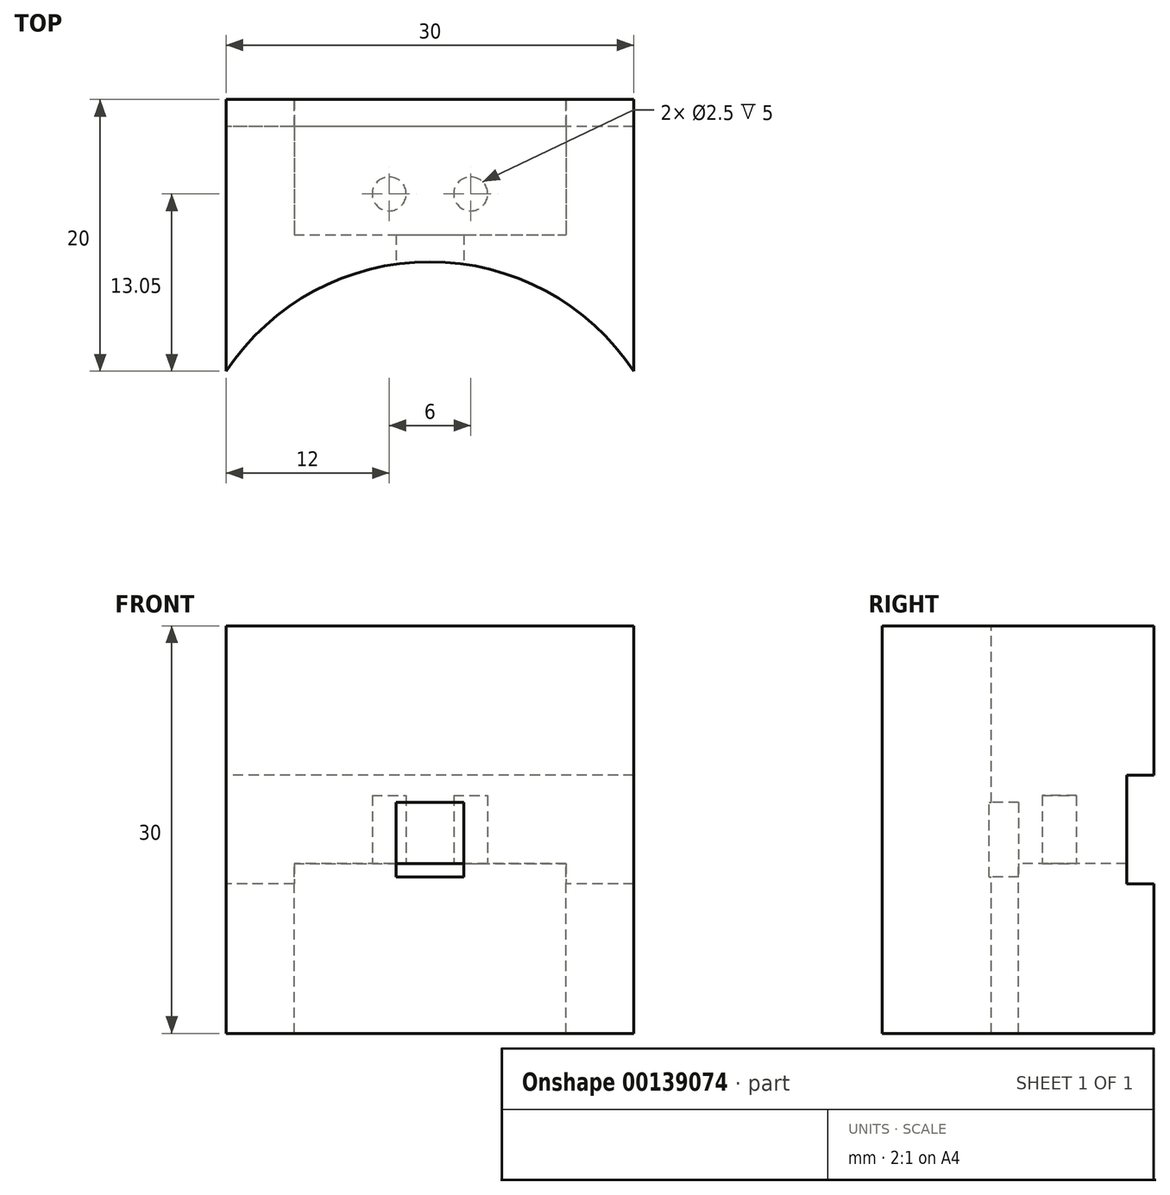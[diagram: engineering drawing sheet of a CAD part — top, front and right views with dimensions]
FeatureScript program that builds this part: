
annotation { "Feature Type Name" : "Feature", "Feature Type Description" : "" }
export const myFeature = defineFeature(function(context is Context, id is Id, definition is map)
    precondition{}
    {
        {
            var Q0;
            Q0=qCreatedBy(makeId("Front.planeOp"),FACE);
            var sketch = newSketch(context, id + "F0", { "sketchPlane" : qUnion([Q0])});
            skLineSegment(sketch, "E0", {"start": v(0, 0) * mm, "end": v(30, 0) * mm});
            skLineSegment(sketch, "E1", {"start": v(30, 0) * mm, "end": v(30, 30) * mm});
            skLineSegment(sketch, "E2", {"start": v(30, 30) * mm, "end": v(0, 30) * mm});
            skLineSegment(sketch, "E3", {"start": v(0, 30) * mm, "end": v(0, 0) * mm});
            skSolve(sketch);
        }
        {
            var Q0;
            Q0 = qSketchRegion(id + "F0", true);
            extrude(context, id + "F1", {"entities" : qUnion([Q0]), "depth" : 20 * mm});
        }
        {
            var Q0;
            Q0=makeQuery(id+"F1.opExtrude","SWEPT_FACE",FACE,{"disambiguationData":[OSD([sQuery(id+"F0.wireOp",EDGE,"E2")])]});
            var sketch = newSketch(context, id + "F2", { "sketchPlane" : qUnion([Q0])});
            skArc(sketch, "E4", {"start": v(30, -20) * mm, "mid": v(15, -11.95) * mm, "end": v(0, -20) * mm});
            skLineSegment(sketch, "E5", {"start": v(0, -20) * mm, "end": v(30, -20) * mm});
            skSolve(sketch);
        }
        {
            var Q0;
            Q0 = qSketchRegion(id + "F2", true);
            extrude(context, id + "F3", {"entities" : qUnion([Q0]), "operationType" : NewBodyOperationType.REMOVE, "endBound" : BoundingType.THROUGH_ALL, "oppositeDirection" : true, "depth" : 25 * mm});
        }
        {
            var Q0;
            Q0=makeQuery(id+"F1.opExtrude","SWEPT_FACE",FACE,{"disambiguationData":[OSD([sQuery(id+"F0.wireOp",EDGE,"E2")])]});
            var sketch = newSketch(context, id + "F4", { "sketchPlane" : qUnion([Q0])});
            skPoint(sketch, "E6", {"position": v(15, -11.95) * mm});
            skSolve(sketch);
        }
        {
            var Q0;
            Q0=qCreatedBy(makeId("Front.planeOp"),FACE);
            var Q1;
            Q1=sQuery(id+"F4.wireOp",VERTEX,"E6");
            cPlane(context, id + "F5", {"entities" : qUnion([Q0, Q1]), "cplaneType" : CPlaneType.PLANE_POINT, "offset" : 25 * mm, "width" : 150 * mm, "height" : 150 * mm});
        }
        {
            var Q0;
            Q0=qCreatedBy(id+"F5.planeOp",FACE);
            cPlane(context, id + "F6", {"entities" : qUnion([Q0]), "cplaneType" : CPlaneType.OFFSET, "offset" : 1 * mm, "width" : 150 * mm, "height" : 150 * mm});
        }
        {
            var Q0;
            Q0=qCreatedBy(id+"F6.planeOp",FACE);
            var sketch = newSketch(context, id + "F7", { "sketchPlane" : qUnion([Q0])});
            skLineSegment(sketch, "E7.bottom", {"start": v(12.5, 17) * mm, "end": v(17.5, 17) * mm});
            skLineSegment(sketch, "E7.top", {"start": v(12.5, 13) * mm, "end": v(17.5, 13) * mm});
            skLineSegment(sketch, "E7.left", {"start": v(12.5, 17) * mm, "end": v(12.5, 13) * mm});
            skLineSegment(sketch, "E7.right", {"start": v(17.5, 17) * mm, "end": v(17.5, 13) * mm});
            skLineSegment(sketch, "E8.0", {"start": v(30, 30) * mm, "end": v(0, 30) * mm, "construction": true});
            skLineSegment(sketch, "E9.0", {"start": v(30, 0) * mm, "end": v(30, 30) * mm, "construction": true});
            skLineSegment(sketch, "E10.0", {"start": v(0, 0) * mm, "end": v(30, 0) * mm, "construction": true});
            skLineSegment(sketch, "E11.0", {"start": v(0, 30) * mm, "end": v(0, 0) * mm, "construction": true});
            skLineSegment(sketch, "E12", {"start": v(15, 0) * mm, "end": v(15, 30) * mm, "construction": true});
            skLineSegment(sketch, "E13", {"start": v(0, 15) * mm, "end": v(30, 15) * mm, "construction": true});
            skSolve(sketch);
        }
        {
            var Q0;
            Q0 = qSketchRegion(id + "F7", true);
            extrude(context, id + "F8", {"entities" : qUnion([Q0]), "operationType" : NewBodyOperationType.REMOVE, "oppositeDirection" : true, "depth" : 3 * mm});
        }
        {
            var Q0;
            Q0=makeQuery(id+"F8.boolean.opBoolean","COPY",FACE,{"derivedFrom":makeQuery(id+"F8.opExtrude","SWEPT_FACE",FACE,{"disambiguationData":[OSD([sQuery(id+"F7.wireOp",EDGE,"E7.top")])]})});
            var sketch = newSketch(context, id + "F9", { "sketchPlane" : qUnion([Q0])});
            skLineSegment(sketch, "E14.0.0", {"start": v(17.5, -12.12) * mm, "end": v(17.5, -9.95) * mm});
            skLineSegment(sketch, "E14.0.1", {"start": v(17.5, -9.95) * mm, "end": v(12.5, -9.95) * mm});
            skLineSegment(sketch, "E14.0.2", {"start": v(12.5, -9.95) * mm, "end": v(12.5, -12.12) * mm});
            skArc(sketch, "E14.0.3", {"start": v(17.5, -12.12) * mm, "mid": v(15, -11.95) * mm, "end": v(12.5, -12.12) * mm});
            skSolve(sketch);
        }
        {
            var Q0;
            Q0 = qSketchRegion(id + "F9", true);
            extrude(context, id + "F10", {"entities" : qUnion([Q0]), "operationType" : NewBodyOperationType.REMOVE, "oppositeDirection" : true, "depth" : 1.5 * mm});
        }
        {
            var Q0;
            Q0=makeQuery(id+"F10.boolean.opBoolean","MERGE",FACE,{"derivedFrom":[makeQuery(id+"F8.boolean.opBoolean","COPY",FACE,{"derivedFrom":makeQuery(id+"F8.opExtrude","CAP_FACE",FACE,{"disambiguationData":[OSD([sQuery(id+"F7.wireOp",EDGE,"E7.bottom"),sQuery(id+"F7.wireOp",EDGE,"E7.top"),sQuery(id+"F7.wireOp",EDGE,"E7.left"),sQuery(id+"F7.wireOp",EDGE,"E7.right")])],"isStart":false})}),makeQuery(id+"F10.opExtrude","SWEPT_FACE",FACE,{"disambiguationData":[OSD([sQuery(id+"F9.wireOp",EDGE,"E14.0.1")])]})]});
            var sketch = newSketch(context, id + "F11", { "sketchPlane" : qUnion([Q0])});
            skLineSegment(sketch, "E15.0", {"start": v(0, 0) * mm, "end": v(30, 0) * mm, "construction": true});
            skLineSegment(sketch, "E16.bottom", {"start": v(5, 0) * mm, "end": v(25, 0) * mm});
            skLineSegment(sketch, "E16.top", {"start": v(5, 12.5) * mm, "end": v(25, 12.5) * mm});
            skLineSegment(sketch, "E16.left", {"start": v(5, 0) * mm, "end": v(5, 12.5) * mm});
            skLineSegment(sketch, "E16.right", {"start": v(25, 0) * mm, "end": v(25, 12.5) * mm});
            skLineSegment(sketch, "E17", {"start": v(15, 11.5) * mm, "end": v(15, 17) * mm, "construction": true});
            skLineSegment(sketch, "E18", {"start": v(15, 12.5) * mm, "end": v(15, 0) * mm, "construction": true});
            skLineSegment(sketch, "E19", {"start": v(15, 0) * mm, "end": v(14.79, 0.06) * mm, "construction": true});
            skSolve(sketch);
        }
        {
            var Q0;
            Q0 = qSketchRegion(id + "F11", true);
            extrude(context, id + "F12", {"entities" : qUnion([Q0]), "operationType" : NewBodyOperationType.REMOVE, "endBound" : BoundingType.THROUGH_ALL, "oppositeDirection" : true, "depth" : 25 * mm});
        }
        {
            var Q0;
            Q0=makeQuery(id+"F0.imprint","IMPRINT",FACE,{"disambiguationData":[TD([[makeQuery(id+"F0.imprint","IMPRINT",EDGE,{"derivedFrom":sQuery(id+"F0.wireOp",EDGE,"E0")}),1.0]])]});
            var sketch = newSketch(context, id + "F13", { "sketchPlane" : qUnion([Q0])});
            skLineSegment(sketch, "E20.0.0", {"start": v(0, 30) * mm, "end": v(0, 0) * mm, "construction": true});
            skLineSegment(sketch, "E20.0.1", {"start": v(0, 0) * mm, "end": v(30, 0) * mm, "construction": true});
            skLineSegment(sketch, "E20.0.2", {"start": v(30, 0) * mm, "end": v(30, 30) * mm, "construction": true});
            skLineSegment(sketch, "E20.0.3", {"start": v(30, 30) * mm, "end": v(0, 30) * mm, "construction": true});
            skLineSegment(sketch, "E21.bottom", {"start": v(30, 19) * mm, "end": v(0, 19) * mm});
            skLineSegment(sketch, "E21.top", {"start": v(30, 11) * mm, "end": v(0, 11) * mm});
            skLineSegment(sketch, "E21.left", {"start": v(30, 19) * mm, "end": v(30, 11) * mm});
            skLineSegment(sketch, "E21.right", {"start": v(0, 19) * mm, "end": v(0, 11) * mm});
            skLineSegment(sketch, "E22", {"start": v(0, 15) * mm, "end": v(30, 15) * mm, "construction": true});
            skSolve(sketch);
        }
        {
            var Q0;
            Q0 = qSketchRegion(id + "F13", true);
            extrude(context, id + "F14", {"entities" : qUnion([Q0]), "operationType" : NewBodyOperationType.REMOVE, "depth" : 2 * mm});
        }
        {
            var Q0;
            Q0=makeQuery(id+"F12.boolean.opBoolean","COPY",FACE,{"derivedFrom":makeQuery(id+"F12.opExtrude","SWEPT_FACE",FACE,{"disambiguationData":[OSD([sQuery(id+"F11.wireOp",EDGE,"E16.top")])]})});
            var sketch = newSketch(context, id + "F15", { "sketchPlane" : qUnion([Q0])});
            skCircle(sketch, "E23", {"center": v(18, 6.95) * mm, "radius": 1.25 * mm});
            skCircle(sketch, "E24", {"center": v(12, 6.95) * mm, "radius": 1.25 * mm});
            skLineSegment(sketch, "E25.0.0", {"start": v(5, 2) * mm, "end": v(25, 2) * mm, "construction": true});
            skLineSegment(sketch, "E25.0.1", {"start": v(25, 2) * mm, "end": v(25, 9.95) * mm, "construction": true});
            skLineSegment(sketch, "E25.0.2", {"start": v(25, 9.95) * mm, "end": v(17.5, 9.95) * mm, "construction": true});
            skLineSegment(sketch, "E25.0.3", {"start": v(17.5, 9.95) * mm, "end": v(12.5, 9.95) * mm, "construction": true});
            skLineSegment(sketch, "E25.0.4", {"start": v(12.5, 9.95) * mm, "end": v(5, 9.95) * mm, "construction": true});
            skLineSegment(sketch, "E25.0.5", {"start": v(5, 9.95) * mm, "end": v(5, 2) * mm, "construction": true});
            skLineSegment(sketch, "E26", {"start": v(15, 2) * mm, "end": v(15, 9.95) * mm, "construction": true});
            skLineSegment(sketch, "E27", {"start": v(18, 6.95) * mm, "end": v(15, 6.95) * mm, "construction": true});
            skLineSegment(sketch, "E28", {"start": v(12, 6.95) * mm, "end": v(15, 6.95) * mm, "construction": true});
            skSolve(sketch);
        }
        {
            var Q0;
            Q0 = qSketchRegion(id + "F15", true);
            extrude(context, id + "F16", {"entities" : qUnion([Q0]), "operationType" : NewBodyOperationType.REMOVE, "oppositeDirection" : true, "depth" : 5 * mm});
        }
    });
